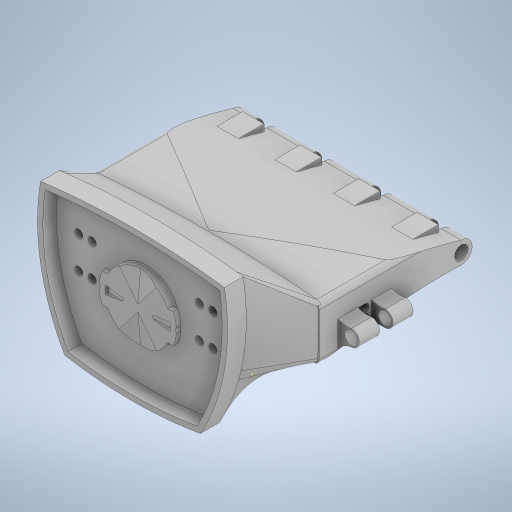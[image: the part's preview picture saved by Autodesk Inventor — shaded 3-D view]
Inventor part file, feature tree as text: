
AUTODESK INVENTOR PART (.ipt)
format: ipt  version: 2023 (Build 270158000, 158)  size: 1,082,368 bytes
history: native  units: in
note: dims shown in document units (in); Inventor stores cm internally (conversion verified against a paired STEP export)
features: sketch x25, extrude x20, other x20, projected_geometry x14, loft x11, plane x6
ambient origin geometry x8: Origin, YZ Plane, XZ Plane, XY Plane, X Axis, Y Axis, Z Axis, Center Point
bodies: Solid1 (feature_tree), Body1 (feature_tree)
feature tree (96):
  extrude  "Extrusion5"  Depth=0.3937in
  sketch  "Sketch5"  dims[d13=0.9843in d18=2.5591in]
  extrude  "Extrusion6"  Depth=2.5591in
  extrude  "Extrusion8"  Depth=0.0787in
  extrude  "Extrusion12"  Depth=1.2795in
  sketch  "Sketch17"  dims[d21=1.2795in d22=1.2795in]
  plane  "Work Plane1"
  extrude  "Extrusion19"  Depth=0.0787in
  loft  "Loft5"
  extrude  "Extrusion20"  Depth=0.6693in TaperAngle=0.0deg
  sketch  "Sketch20"  dims[d27=0.0787in d28=0.0in d31=0.6693in d32=0.0in]
  plane  "Work Plane3"
  extrude  "Extrusion21"  Depth=0.7874in
  plane  "Work Plane4"
  extrude  "Extrusion22"  Depth=0.0787in
  sketch  "Sketch23"  dims[d116=0.0197in d117=0.0787in]
  extrude  "Extrusion23"  Depth=0.0787in
  extrude  "Extrusion24"  TaperAngle=0.0deg  [1 undecoded]
  extrude  "Extrusion26"  Depth=2.2047in TaperAngle=0.0deg
  loft  "Loft15"
  loft  "Loft16"
  loft  "Loft17"
  loft  "Loft18"
  loft  "Loft19"
  loft  "Loft20"
  loft  "Loft21"
  loft  "Loft22"
  extrude  "Extrusion32"  Depth=0.0591in
  extrude  "Extrusion33"  Depth=0.1969in
  extrude  "Extrusion34"  Depth=0.2559in
  extrude  "Extrusion35"  Depth=0.2559in
  extrude  "Extrusion36"  Depth=0.1181in
  extrude  "Extrusion37"  Depth=0.1181in
  extrude  "Extrusion38"  Depth=0.1181in
  sketch  "Sketch36"  dims[d144=0.0394in d145=0.2953in]
  extrude  "Extrusion39"  Depth=0.3937in TaperAngle=0.0deg
  plane  "Work Plane6"
  sketch  "Sketch38"  dims[d148=0.0591in d149=0.2953in]
  plane  "Work Plane7"
  sketch  "Sketch39"  dims[d150=0.1969in d152=0.2953in]
  plane  "Work Plane8"
  extrude  "Extrusion40"  Depth=0.1181in
  loft  "Loft25"
  loft  "Loft26"
  sketch  "Sketch1"  dims[d10=0.3937in d11=0.0in d12=0.9055in]
  sketch  "Sketch8"  dims[d19=0.0787in d20=0.0787in]
  sketch  "Sketch18"  dims[d23=0.0787in d24=0.0787in]
  other  "Edges9"
  other  "Edges10"
  sketch  "Sketch19"  dims[d25=2.5591in d26=1.8898in]
  projected_geometry  "Projected Loop2"
  sketch  "Sketch21"  dims[d54=0.0787in d55=0.0in d106=0.7874in]
  projected_geometry  "Projected Loop3"
  projected_geometry  "Projected Loop4"
  sketch  "Sketch22"  dims[d108=1.6732in d112=0.0787in]
  sketch  "Sketch24"  dims[d118=0.0394in d119=0.0in d120=0.0in d121=90.0deg]
  other  "Edges29"
  other  "Edges30"
  other  "Edges31"
  other  "Edges32"
  other  "Edges33"
  other  "Edges34"
  other  "Edges35"
  other  "Edges36"
  other  "Edges37"
  other  "Edges38"
  other  "Edges39"
  other  "Edges40"
  other  "Edges41"
  other  "Edges42"
  other  "Edges43"
  other  "Edges44"
  sketch  "Sketch26"  dims[d122=0.0in d123=90.0deg d124=2.2047in d125=0.0in]
  sketch  "Sketch30"  dims[d127=0.1969in d132=6.8898in]
  projected_geometry  "Projected Loop8"
  sketch  "Sketch31"  dims[d133=6.8898in d134=0.0in d135=0.0in]
  projected_geometry  "Projected Loop9"
  sketch  "Sketch32"  dims[d136=0.2953in d137=0.1969in]
  sketch  "Sketch33"  dims[d138=0.2953in d139=0.0591in]
  projected_geometry  "Projected Loop10"
  sketch  "Sketch34"  dims[d140=0.2953in d141=0.1969in]
  sketch  "Sketch35"  dims[d142=0.2953in d143=0.0394in]
  projected_geometry  "Projected Loop11"
  projected_geometry  "Projected Loop12"
  projected_geometry  "Projected Loop13"
  projected_geometry  "Projected Loop14"
  sketch  "Sketch37"  dims[d146=0.1969in d147=0.2953in]
  projected_geometry  "Projected Loop15"
  projected_geometry  "Projected Loop16"
  projected_geometry  "Projected Loop17"
  projected_geometry  "Projected Loop18"
  sketch  "Sketch40"  dims[d153=0.2559in d154=0.2559in]
  sketch  "Sketch41"  dims[d155=0.2559in d156=0.2559in]
  other  "Edges49"
  sketch  "Sketch42"  dims[d158=0.2559in d159=0.2559in d160=0.2559in d161=0.0394in d162=0.3937in d163=0.0in d164=0.0394in d165=0.0787in d166=0.2756in d167=0.0394in d168=0.0787in d169=0.2756in d170=0.0394in d171=0.0787in d172=0.2756in d173=0.0787in d174=0.0394in d175=0.0787in d176=0.2756in d177=0.0787in d178=0.0197in d179=0.0197in d180=0.0197in d181=0.0197in d182=0.1181in d184=0.1181in d185=0.3937in d186=0.0in d187=0.3937in d188=0.0in d191=0.5512in d193=0.5512in d218=0.1181in d219=0.1181in d220=0.1181in d221=0.1181in d222=0.1181in d223=0.1181in d224=0.1181in d225=0.1181in d226=0.1969in d227=0.0in d228=0.3937in d229=0.3937in d230=0.3937in d231=0.3937in d232=0.0787in d233=0.0787in d234=0.0787in d235=0.0787in d240=0.7874in d241=0.9843in d242=0.7874in d243=0.9843in d276=0.7874in d277=0.9843in d278=0.7874in d279=0.9843in d280=0.0in d281=90.0deg d282=0.0in d283=90.0deg d284=0.0in d285=90.0deg d286=0.0in d287=90.0deg d288=0.0in d289=90.0deg d290=0.0in d291=90.0deg d292=0.0in d293=90.0deg d294=0.0in d295=90.0deg d296=0.0in d297=90.0deg d298=0.0in d299=90.0deg d300=0.0in d301=90.0deg d302=0.0in d303=90.0deg d304=0.0in d305=90.0deg d306=0.0in d307=90.0deg d308=0.0in d309=90.0deg d310=0.0in d311=90.0deg d312=0.2756in d313=0.7874in d314=0.2953in d315=0.2953in d316=0.1969in d333=0.3937in d334=0.0in d335=0.2362in d336=0.1969in d337=0.3181in d338=0.3181in d340=0.1378in d341=0.3937in d342=0.0in d344=0.3937in d345=0.0in d346=0.3937in d347=0.0in d348=0.3937in d349=0.0in d351=0.1181in d352=0.1181in d353=0.1969in d354=0.0in d356=0.1181in d358=0.1181in d367=0.1575in d368=0.0in d369=0.1575in d370=0.0in d371=0.3937in d372=0.0in d373=0.1181in d374=0.0in d375=90.0deg d376=0.0in d377=90.0deg d378=0.1181in d379=0.0in d380=90.0deg d381=0.0in d382=90.0deg d0=0.0197in d1=1.9685in d2=0.0197in d3=1.9685in d76=0.0197in d77=1.9685in d78=0.0197in d79=1.9685in d192=1.9685in d194=1.9685in d329=0.0197in d330=1.9685in d331=0.0197in d332=1.9685in d339=0.0197in]
  other  "Edges50"
note: 1 required parameter value undecoded (feature->parameter linkage not recoverable at this tier; creation-order binding heuristic only, values carry confidence <= 0.55)
